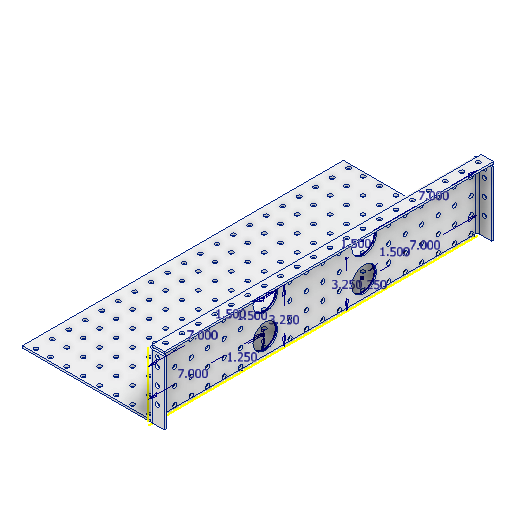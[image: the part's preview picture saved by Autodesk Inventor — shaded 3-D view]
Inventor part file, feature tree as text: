
AUTODESK INVENTOR PART (.ipt)
format: ipt  version: 2022 (Build 260153000, 153)  size: 991,744 bytes
history: native  units: in
note: dims shown in document units (in); Inventor stores cm internally (conversion verified against a paired STEP export)
features: other x17, sketch x15, sheet_metal_op x13, pattern_linear x8
ambient origin geometry x8: Origin, YZ Plane, XZ Plane, XY Plane, X Axis, Y Axis, Z Axis, Center Point
bodies: Solid1 (feature_tree)
feature tree (53):
  sheet_metal_op  "Face1"
  sheet_metal_op  "Flange1"
  sheet_metal_op  "Flange2"
  sketch  "Sketch4"  dims[d3=0.125in]
  pattern_linear  "Rectangular Pattern2"  Spacing1=8.0in  [1 undecoded]
  pattern_linear  "Rectangular Pattern3"  Spacing1=0.5in  [1 undecoded]
  pattern_linear  "Rectangular Pattern4"  Spacing1=0.125in  [1 undecoded]
  pattern_linear  "Rectangular Pattern5"  Spacing1=0.125in  [1 undecoded]
  pattern_linear  "Rectangular Pattern6"  Spacing1=1.5in  [1 undecoded]
  pattern_linear  "Rectangular Pattern7"  Spacing1=3.25in  [1 undecoded]
  sheet_metal_op  "Flange3"
  sheet_metal_op  "Flange4"
  pattern_linear  "Rectangular Pattern11"  Spacing1=1.5in  [1 undecoded]
  pattern_linear  "Rectangular Pattern12"  Spacing1=3.25in  [1 undecoded]
  sketch  "Sketch1"  dims[d0=4.375in]
  other  "Plate1"
  sketch  "Sketch2"  dims[d1=20.0in]
  other  "Plate2"
  sheet_metal_op  "Bend1"
  sheet_metal_op  "Corner1"
  sketch  "Sketch3"  dims[d2=0.125in]
  other  "Plate3"
  sheet_metal_op  "Bend2"
  sheet_metal_op  "Corner2"
  sketch  "Sketch5"  dims[d4=0.0625in]
  sketch  "Sketch7"  dims[d5=0.25in]
  sketch  "Sketch8"  dims[d6=0.125in]
  sketch  "Sketch9"  dims[d7=1.0in d8=90.0deg d9=0.125in]
  other  "Plate4"
  sheet_metal_op  "Bend3"
  sheet_metal_op  "Corner3"
  sketch  "Sketch11"  dims[d10=0.5in]
  other  "Plate5"
  sheet_metal_op  "Bend4"
  sheet_metal_op  "Corner4"
  sketch  "Sketch12"  dims[d11=0.125in]
  sketch  "Sketch15"  dims[d12=0.125in]
  sketch  "Sketch16"  dims[d13=0.125in]
  sketch  "Sketch17"  dims[d14=0.0625in]
  sketch  "Sketch18"  dims[d15=0.25in]
  sketch  "Sketch20"  dims[d16=0.125in d17=8.0in d18=90.0deg d19=0.125in d20=0.5in d21=0.125in d22=0.125in d24=1.5in d26=3.25in d27=1.5in d28=3.25in d32=1.5in d34=1.25in d35=1.5in d37=1.25in d41=0.5in d43=0.125in d44=0.0in d48=0.26in d50=0.5in d51=0.125in d52=0.0in d53=7.874in d55=1.0in d56=0.435in d57=0.26in d58=0.26in d59=0.26in d60=0.26in d61=1.0in d62=1.0in d63=1.0in d64=0.375in d65=0.5in d66=0.26in d67=0.5in d68=0.5in d69=0.26in d70=0.375in d71=0.5in d72=0.26in d73=0.26in d74=1.0in d75=1.0in d76=0.26in d77=1.0in d78=0.26in d79=0.5in d80=0.5in d81=0.125in d82=0.0in d83=2.3622in d85=1.0in d86=2.3622in d88=1.0in d89=7.0in d90=7.0in d91=7.0in d92=7.0in d93=0.125in d94=0.0in d97=0.125in d98=0.0in d99=1.5748in d101=1.0in d102=1.1811in d104=1.0in d105=0.7874in d107=1.0in d108=1.5748in d110=1.0in d111=0.7874in d113=3.5in d114=1.1811in d116=1.0in d117=0.7874in d119=1.0in d120=0.125in d121=0.0625in d122=0.25in d123=0.125in d124=1.0in d125=90.0deg d126=0.125in d127=0.5in d128=0.125in d129=0.125in d130=0.125in d131=0.0625in d132=0.25in d133=0.125in d134=1.0in d135=90.0deg d136=0.125in d137=0.5in d138=0.125in d139=0.125in d140=0.125in d141=0.0in d156=0.26in d157=0.435in d158=1.125in d161=0.26in d162=1.0in d163=0.26in d164=2.0in d165=0.125in d166=0.0in d167=0.26in d168=1.125in d169=0.435in d170=0.26in d171=1.0in d172=0.26in d173=1.0in d174=0.125in d175=0.0in d179=0.26in d180=0.485in d181=0.435in d182=0.125in d183=0.0in d184=0.26in d185=0.435in d186=0.485in d187=0.125in d188=0.0in d203=1.435in d204=2.7559in d206=1.0in d207=7.874in d209=1.0in d210=0.25in d211=0.25in d212=7.75in d213=0.26in d214=0.25in d216=6.875in d217=0.125in d218=0.0in d219=7.874in d221=1.0in d222=0.26in d223=0.375in]
  other  "Cut2"
  other  "Cut3"
  other  "Cut4"
  other  "Cut5"
  other  "Cut6"
  other  "Cut7"
  other  "Cut10"
  other  "Cut11"
  other  "Cut12"
  other  "Cut13"
  other  "Cut15"
  other  "Definition1"
note: 8 required parameter values undecoded (feature->parameter linkage not recoverable at this tier; creation-order binding heuristic only, values carry confidence <= 0.55)
